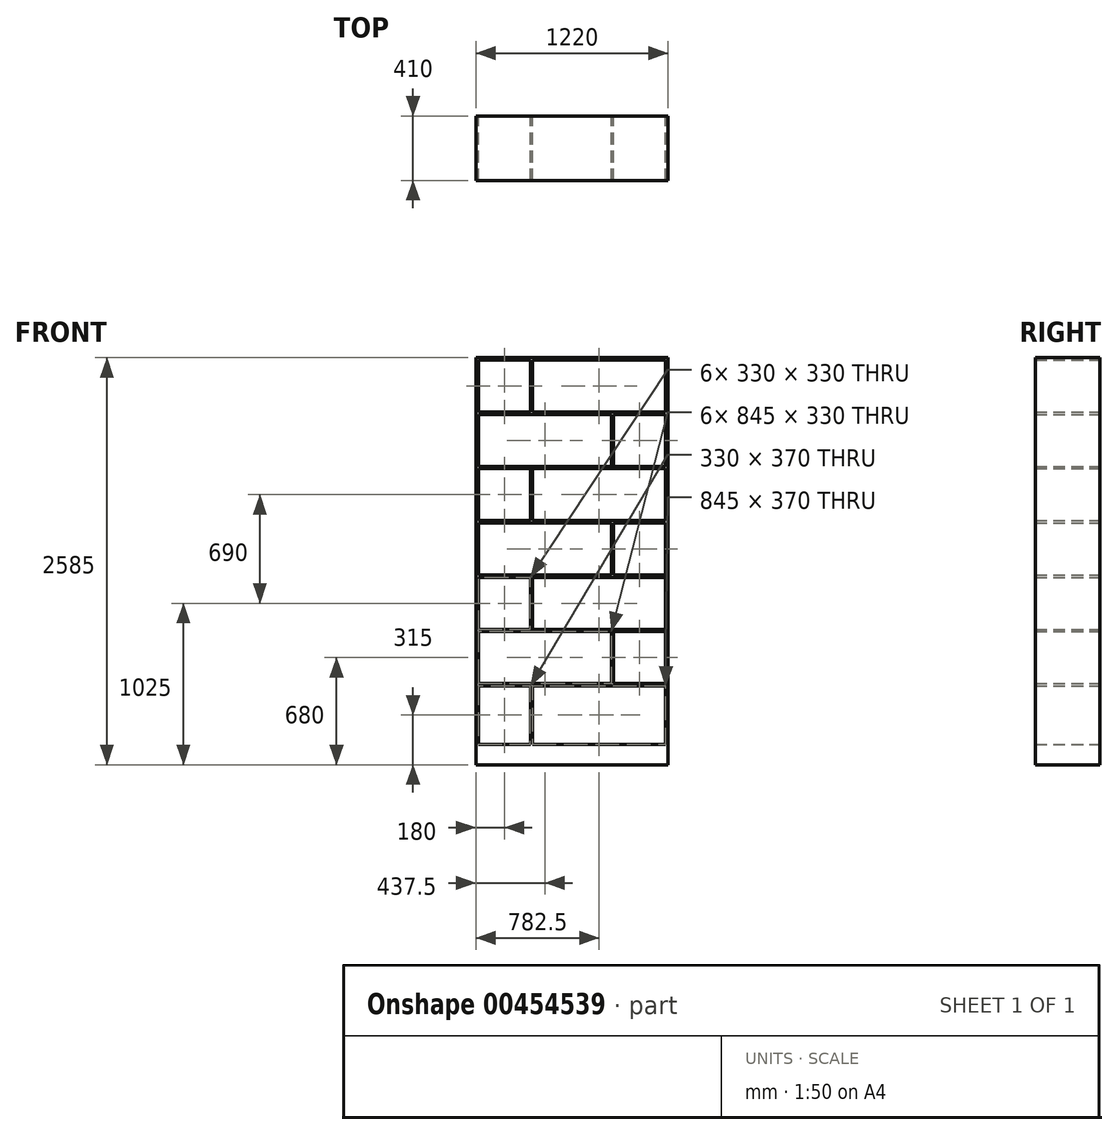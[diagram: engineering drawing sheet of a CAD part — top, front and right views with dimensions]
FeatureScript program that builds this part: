
annotation { "Feature Type Name" : "Feature", "Feature Type Description" : "" }
export const myFeature = defineFeature(function(context is Context, id is Id, definition is map)
    precondition{}
    {
        {
            var Q0;
            Q0=qCreatedBy(makeId("Front.planeOp"),FACE);
            var sketch = newSketch(context, id + "F0", { "sketchPlane" : qUnion([Q0])});
            skLineSegment(sketch, "E0.bottom", {"start": v(0, 0) * mm, "end": v(1220, 0) * mm});
            skLineSegment(sketch, "E0.top", {"start": v(0, 2585) * mm, "end": v(1220, 2585) * mm});
            skLineSegment(sketch, "E0.left", {"start": v(0, 0) * mm, "end": v(0, 2585) * mm});
            skLineSegment(sketch, "E0.right", {"start": v(1220, 0) * mm, "end": v(1220, 2585) * mm});
            skLineSegment(sketch, "E1.bottom", {"start": v(15, 2570) * mm, "end": v(345, 2570) * mm});
            skLineSegment(sketch, "E1.top", {"start": v(15, 2240) * mm, "end": v(345, 2240) * mm});
            skLineSegment(sketch, "E1.left", {"start": v(15, 2570) * mm, "end": v(15, 2240) * mm});
            skLineSegment(sketch, "E1.right", {"start": v(345, 2570) * mm, "end": v(345, 2240) * mm});
            skLineSegment(sketch, "E2.bottom", {"start": v(1205, 2570) * mm, "end": v(360, 2570) * mm});
            skLineSegment(sketch, "E2.top", {"start": v(1205, 2240) * mm, "end": v(360, 2240) * mm});
            skLineSegment(sketch, "E2.left", {"start": v(1205, 2570) * mm, "end": v(1205, 2240) * mm});
            skLineSegment(sketch, "E2.right", {"start": v(360, 2570) * mm, "end": v(360, 2240) * mm});
            skLineSegment(sketch, "E3.bottom", {"start": v(875, 2225) * mm, "end": v(1205, 2225) * mm});
            skLineSegment(sketch, "E3.top", {"start": v(875, 1895) * mm, "end": v(1205, 1895) * mm});
            skLineSegment(sketch, "E3.left", {"start": v(875, 2225) * mm, "end": v(875, 1895) * mm});
            skLineSegment(sketch, "E3.right", {"start": v(1205, 2225) * mm, "end": v(1205, 1895) * mm});
            skLineSegment(sketch, "E4.bottom", {"start": v(15, 2225) * mm, "end": v(860, 2225) * mm});
            skLineSegment(sketch, "E4.top", {"start": v(15, 1895) * mm, "end": v(860, 1895) * mm});
            skLineSegment(sketch, "E4.left", {"start": v(15, 2225) * mm, "end": v(15, 1895) * mm});
            skLineSegment(sketch, "E4.right", {"start": v(860, 2225) * mm, "end": v(860, 1895) * mm});
            skLineSegment(sketch, "E5.bottom", {"start": v(15, 1880) * mm, "end": v(345, 1880) * mm});
            skLineSegment(sketch, "E5.top", {"start": v(15, 1550) * mm, "end": v(345, 1550) * mm});
            skLineSegment(sketch, "E5.left", {"start": v(15, 1880) * mm, "end": v(15, 1550) * mm});
            skLineSegment(sketch, "E5.right", {"start": v(345, 1880) * mm, "end": v(345, 1550) * mm});
            skLineSegment(sketch, "E6.bottom", {"start": v(360, 1880) * mm, "end": v(1205, 1880) * mm});
            skLineSegment(sketch, "E6.top", {"start": v(360, 1550) * mm, "end": v(1205, 1550) * mm});
            skLineSegment(sketch, "E6.left", {"start": v(360, 1880) * mm, "end": v(360, 1550) * mm});
            skLineSegment(sketch, "E6.right", {"start": v(1205, 1880) * mm, "end": v(1205, 1550) * mm});
            skLineSegment(sketch, "E7.bottom", {"start": v(875, 1535) * mm, "end": v(1205, 1535) * mm});
            skLineSegment(sketch, "E7.top", {"start": v(875, 1205) * mm, "end": v(1205, 1205) * mm});
            skLineSegment(sketch, "E7.left", {"start": v(875, 1535) * mm, "end": v(875, 1205) * mm});
            skLineSegment(sketch, "E7.right", {"start": v(1205, 1535) * mm, "end": v(1205, 1205) * mm});
            skLineSegment(sketch, "E8.bottom", {"start": v(15, 1535) * mm, "end": v(860, 1535) * mm});
            skLineSegment(sketch, "E8.top", {"start": v(15, 1205) * mm, "end": v(860, 1205) * mm});
            skLineSegment(sketch, "E8.left", {"start": v(15, 1535) * mm, "end": v(15, 1205) * mm});
            skLineSegment(sketch, "E8.right", {"start": v(860, 1535) * mm, "end": v(860, 1205) * mm});
            skLineSegment(sketch, "E9.bottom", {"start": v(15, 1190) * mm, "end": v(345, 1190) * mm});
            skLineSegment(sketch, "E9.top", {"start": v(15, 860) * mm, "end": v(345, 860) * mm});
            skLineSegment(sketch, "E9.left", {"start": v(15, 1190) * mm, "end": v(15, 860) * mm});
            skLineSegment(sketch, "E9.right", {"start": v(345, 1190) * mm, "end": v(345, 860) * mm});
            skLineSegment(sketch, "E10.bottom", {"start": v(360, 1190) * mm, "end": v(1205, 1190) * mm});
            skLineSegment(sketch, "E10.top", {"start": v(360, 860) * mm, "end": v(1205, 860) * mm});
            skLineSegment(sketch, "E10.left", {"start": v(360, 1190) * mm, "end": v(360, 860) * mm});
            skLineSegment(sketch, "E10.right", {"start": v(1205, 1190) * mm, "end": v(1205, 860) * mm});
            skLineSegment(sketch, "E11.bottom", {"start": v(875, 845) * mm, "end": v(1205, 845) * mm});
            skLineSegment(sketch, "E11.top", {"start": v(875, 515) * mm, "end": v(1205, 515) * mm});
            skLineSegment(sketch, "E11.left", {"start": v(875, 845) * mm, "end": v(875, 515) * mm});
            skLineSegment(sketch, "E11.right", {"start": v(1205, 845) * mm, "end": v(1205, 515) * mm});
            skLineSegment(sketch, "E12.bottom", {"start": v(15, 845) * mm, "end": v(860, 845) * mm});
            skLineSegment(sketch, "E12.top", {"start": v(15, 515) * mm, "end": v(860, 515) * mm});
            skLineSegment(sketch, "E12.left", {"start": v(15, 845) * mm, "end": v(15, 515) * mm});
            skLineSegment(sketch, "E12.right", {"start": v(860, 845) * mm, "end": v(860, 515) * mm});
            skLineSegment(sketch, "E13.bottom", {"start": v(15, 500) * mm, "end": v(345, 500) * mm});
            skLineSegment(sketch, "E13.top", {"start": v(15, 130) * mm, "end": v(345, 130) * mm});
            skLineSegment(sketch, "E13.left", {"start": v(15, 500) * mm, "end": v(15, 130) * mm});
            skLineSegment(sketch, "E13.right", {"start": v(345, 500) * mm, "end": v(345, 130) * mm});
            skLineSegment(sketch, "E14.bottom", {"start": v(360, 500) * mm, "end": v(1205, 500) * mm});
            skLineSegment(sketch, "E14.top", {"start": v(360, 130) * mm, "end": v(1205, 130) * mm});
            skLineSegment(sketch, "E14.left", {"start": v(360, 500) * mm, "end": v(360, 130) * mm});
            skLineSegment(sketch, "E14.right", {"start": v(1205, 500) * mm, "end": v(1205, 130) * mm});
            skSolve(sketch);
        }
        {
            var Q0;
            Q0 = qSketchRegion(id + "F0", true);
            extrude(context, id + "F1", {"entities" : qUnion([Q0]), "depth" : 410 * mm});
        }
    });
